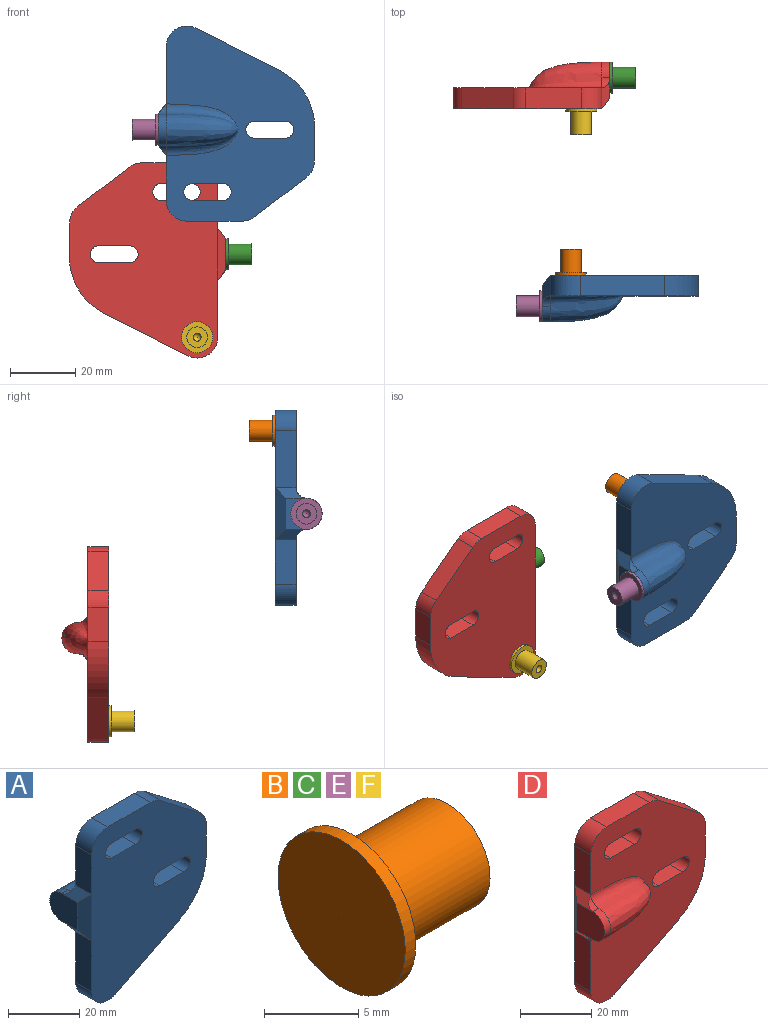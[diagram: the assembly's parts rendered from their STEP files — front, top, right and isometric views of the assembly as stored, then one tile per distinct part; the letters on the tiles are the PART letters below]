
ASSEMBLY  parts=6 mates=5
PART A: 29 faces, bbox 48.8x15.3x60.7 mm
  f0: plane 13.67x6.35mm, normal (-1,0,0), area 86.8mm2, adj f1,f14,f20,f28
  f1: plane 59.81x45.52mm, normal (0,1,0), area 1734.1mm2, adj f0,f2,f3,f4,f5,f6,f7,f8
  f2: plane 9.53x6.35mm, normal (0,0,-1), area 60.5mm2, adj f1,f3,f19,f20
  f3: cylinder r=2.55mm len=6.35mm, axis (0,-1,0), area 50.9mm2, adj f1,f2,f4,f20
  f4: plane 9.53x6.35mm, normal (0,0,1), area 60.5mm2, adj f1,f3,f19,f20
  f5: plane 9.53x6.35mm, normal (0,0,-1), area 60.5mm2, adj f1,f6,f17,f20
  f6: cylinder r=2.55mm len=6.35mm, axis (0,-1,0), area 50.9mm2, adj f1,f5,f7,f20
  f7: plane 9.53x6.35mm, normal (0,0,1), area 60.5mm2, adj f1,f6,f17,f20
  f8: cylinder r=19.05mm len=16.99mm, axis (0,-1,0), area 133.2mm2, adj f1,f9,f18,f20
  f9: plane 10.56x6.35mm, normal (1,0,0), area 67.1mm2, adj f1,f8,f10,f20
  f10: cylinder r=6.35mm len=6.35mm, axis (0,-1,0), area 37.1mm2, adj f1,f9,f11,f20
  f11: plane 15.81x12.05mm, normal (0.61,0,0.8), area 126.2mm2, adj f1,f10,f12,f20
  f12: cylinder r=6.35mm len=6.35mm, axis (0,-1,0), area 26.3mm2, adj f1,f11,f13,f20
  f13: plane 16.91x6.35mm, normal (0,0,1), area 107.4mm2, adj f1,f12,f14,f20
  f14: cylinder r=6.35mm len=6.35mm, axis (0,-1,0), area 63.3mm2, adj f0,f1,f13,f20
  f15: plane 17.46x6.35mm, normal (-1,0,0), area 110.9mm2, adj f1,f16,f20,f26
  f16: cylinder r=6.35mm len=9.22mm, axis (0,-1,0), area 82.3mm2, adj f1,f15,f18,f20
  f17: cylinder r=2.55mm len=6.35mm, axis (0,-1,0), area 50.9mm2, adj f1,f5,f7,f20
  f18: plane 25.76x13.07mm, normal (0.45,0,-0.89), area 183.4mm2, adj f1,f8,f16,f20
  f19: cylinder r=2.55mm len=6.35mm, axis (0,-1,0), area 50.9mm2, adj f1,f2,f4,f20
  f20: plane 59.7x45.42mm, normal (0,-1,0), area 2020.6mm2, adj f0,f2,f3,f4,f5,f6,f7,f8
  f21: bspline ~22.23x15.88mm, area 466.9mm2, adj f1,f22,f23,f24
  f22: cylinder r=3.17mm len=3.18mm, axis (1,0,0), area 5.9mm2, adj f21,f23,f26
  f23: cylinder r=4.76mm len=9.53mm, axis (1,0,0), area 35.6mm2, adj f21,f22,f24,f25
  f24: cylinder r=3.17mm len=3.18mm, axis (1,0,0), area 5.9mm2, adj f21,f23,f28
  f25: plane 11.11x9.53mm, normal (-1,0,0), area 96.1mm2, adj f23,f26,f27,f28
  f26: plane 10.53x4.18mm, normal (-0.8,0,-0.6), area 21.6mm2, adj f15,f22,f25,f27
  f27: plane 15.88x3.18mm, normal (-0.8,-0.6,0), area 50.4mm2, adj f20,f25,f26,f28
  f28: plane 10.53x4.18mm, normal (-0.8,0,0.6), area 21.6mm2, adj f0,f24,f25,f27
PART B: 7 faces, bbox 7.9x9.5x9.5 mm
  f0: sphere r=1.19mm, area 8.9mm2, adj f1,f6
  f1: plane 6.35x6.35mm, normal (1,0,0), area 27.2mm2, adj f0,f2
  f2: cylinder r=3.17mm len=7.14mm, axis (-1,0,0), area 142.5mm2, adj f1,f3
  f3: plane 9.53x9.53mm, normal (1,0,0), area 39.6mm2, adj f2,f4
  f4: cylinder r=4.76mm len=9.53mm, axis (-1,0,0), area 23.8mm2, adj f3,f5
  f5: plane 9.53x9.53mm, normal (-1,0,0), area 71.3mm2, adj f4,f6
  f6: cylinder r=0.01mm len=6.75mm, axis (-1,0,0), area 0.5mm2, adj f0,f5
PART C: same geometry as B
PART D: 29 faces, bbox 48.8x15.3x60.7 mm
  f0: plane 13.67x6.35mm, normal (-1,0,0), area 86.8mm2, adj f1,f14,f20,f28
  f1: plane 59.81x45.52mm, normal (0,-1,0), area 1734.1mm2, adj f0,f2,f3,f4,f5,f6,f7,f8
  f2: plane 9.53x6.35mm, normal (0,0,-1), area 60.5mm2, adj f1,f3,f19,f20
  f3: cylinder r=2.55mm len=6.35mm, axis (0,1,0), area 50.9mm2, adj f1,f2,f4,f20
  f4: plane 9.53x6.35mm, normal (0,0,1), area 60.5mm2, adj f1,f3,f19,f20
  f5: plane 9.53x6.35mm, normal (0,0,-1), area 60.5mm2, adj f1,f6,f17,f20
  f6: cylinder r=2.55mm len=6.35mm, axis (0,1,0), area 50.9mm2, adj f1,f5,f7,f20
  f7: plane 9.53x6.35mm, normal (0,0,1), area 60.5mm2, adj f1,f6,f17,f20
  f8: cylinder r=19.05mm len=16.99mm, axis (0,1,0), area 133.2mm2, adj f1,f9,f18,f20
  f9: plane 10.56x6.35mm, normal (1,0,0), area 67.1mm2, adj f1,f8,f10,f20
  f10: cylinder r=6.35mm len=6.35mm, axis (0,1,0), area 37.1mm2, adj f1,f9,f11,f20
  f11: plane 15.81x12.05mm, normal (0.61,0,0.8), area 126.2mm2, adj f1,f10,f12,f20
  f12: cylinder r=6.35mm len=6.35mm, axis (0,1,0), area 26.3mm2, adj f1,f11,f13,f20
  f13: plane 16.91x6.35mm, normal (0,0,1), area 107.4mm2, adj f1,f12,f14,f20
  f14: cylinder r=6.35mm len=6.35mm, axis (0,1,0), area 63.3mm2, adj f0,f1,f13,f20
  f15: plane 17.46x6.35mm, normal (-1,0,0), area 110.9mm2, adj f1,f16,f20,f26
  f16: cylinder r=6.35mm len=9.22mm, axis (0,1,0), area 82.3mm2, adj f1,f15,f18,f20
  f17: cylinder r=2.55mm len=6.35mm, axis (0,1,0), area 50.9mm2, adj f1,f5,f7,f20
  f18: plane 25.76x13.07mm, normal (0.45,0,-0.89), area 183.4mm2, adj f1,f8,f16,f20
  f19: cylinder r=2.55mm len=6.35mm, axis (0,1,0), area 50.9mm2, adj f1,f2,f4,f20
  f20: plane 59.7x45.42mm, normal (0,1,0), area 2020.6mm2, adj f0,f2,f3,f4,f5,f6,f7,f8
  f21: bspline ~22.23x15.88mm, area 466.9mm2, adj f1,f22,f23,f24
  f22: cylinder r=3.17mm len=3.18mm, axis (1,0,0), area 5.9mm2, adj f21,f23,f26
  f23: cylinder r=4.76mm len=9.53mm, axis (1,0,0), area 35.6mm2, adj f21,f22,f24,f25
  f24: cylinder r=3.17mm len=3.18mm, axis (1,0,0), area 5.9mm2, adj f21,f23,f28
  f25: plane 11.11x9.53mm, normal (-1,0,0), area 96.1mm2, adj f23,f26,f27,f28
  f26: plane 10.53x4.18mm, normal (-0.8,0,-0.6), area 21.6mm2, adj f15,f22,f25,f27
  f27: plane 15.88x3.18mm, normal (-0.8,0.6,0), area 50.4mm2, adj f20,f25,f26,f28
  f28: plane 10.53x4.18mm, normal (-0.8,0,0.6), area 21.6mm2, adj f0,f24,f25,f27
PART E: same geometry as B
PART F: same geometry as B
PLACE A rot(axis=(1,0,0),180deg) t=(54.15,9.09,47.99)mm
PLACE B rot(axis=(-0.71,-0.71,0),180deg) t=(60.5,9.09,60.69)mm
PLACE C rot(axis=(1,0,0),180deg) t=(72.41,69.62,-2.81)mm
PLACE D rot(axis=(0,0,1),180deg) t=(70.03,60.1,-15.51)mm
PLACE E rot(axis=(0,0,1),180deg) t=(51.77,-0.44,35.29)mm
PLACE F rot(axis=(0.71,-0.71,0),180deg) t=(63.68,60.1,-28.21)mm
MATE slider D.f19 <-> A.f19  axis (0,-1,0) through (62.09,60.1,16.24)mm
MATE fastened B.f2 <-> A.f16  axis (0,-1,0) through (60.5,9.09,60.69)mm
MATE fastened C.f6 <-> D.f23  axis (-1,0,0) through (72.41,69.62,-2.81)mm
MATE fastened A.f23 <-> E.f2  axis (-1,0,0) through (51.77,-0.44,35.29)mm
MATE fastened F.f2 <-> D.f16  axis (0,1,0) through (63.68,60.1,-28.21)mm
